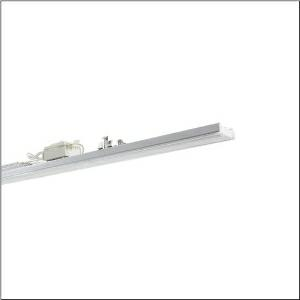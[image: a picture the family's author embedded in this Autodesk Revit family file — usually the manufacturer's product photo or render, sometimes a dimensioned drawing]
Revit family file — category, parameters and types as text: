
# Revit family: licross_r__21_recessed_mo_52tl1edn48xg_af32
name_source: partatom
category: Lighting Fixtures
units: mm (PartAtom-declared; Revit-internal decimal feet)

## family parameters
Cut with Voids When Loaded = No
Host = Face
Light Source = No
Part Type = Normal
Room Calculation Point = No
Round Connector Dimension = Use Diameter
Shared = No

## types (1)
- --- (1 x LED, 8000 lm, 45.8 W, 4000K)
    Apparent Load = 46 VA
    CIE Flux Codes = 85 95 99 100 100
    Color Rendering = 80
    Color Temperature = 4000K
    Default Elevation = 1800 mm
    Description = Licross® 21 Recessed MO, luminaire insert, of sheet steel, galvanised, coil coated, white, length: 1.500mm, width: 66mm, height: 67mm, LED rated luminous flux: 8.000lm, light colour: 840, control gear: DALI 2, with plug, 5-pole, with phase selection, mains connection: 220..240V, AC, 50/60Hz, rated input power: 46W, halogen-free wiring, primary light control with lens, of plastic, primary optical cover: cover, of PMMA, light emission: direct distribution, primary light characteristic: symmetric, protection rating (complete): IP40, insulation class (complete): insulation class I (protective earthing), certification: CE, ENEC, VDE, UKCA, protection symbol: D if used in an environment without relevant dust loads with corresponding accessories, impact resistance: IK06, permissible ambient temperature for indoor applications: -25..+40°C, corresponds to IFS (International Featured Standards) requirements for safety and quality in the food industry, reducing of maximum allowable ambient temperature of 5°C with ceiling mounting, LABS conformity tested according to VDMA 24364:2018-05, packaging unit: 1 piece
    Height = 58 mm
    Lamp = 1 x LED
    Lamp Light Flux = 8000 lm
    Lamp Power = 45.8 W
    Lamp count = 1
    Length = 1500 mm
    Luminous efficacy = 175 lm/W
    Manufacturer = Siteco
    ModVariant = No
    Model = 52TL1EDN48XG
    Mounting Place = Ceiling
    Mounting Type = Pendant
    Number of Poles = 1
    OnlyDefault = Yes
    Power Factor = 1
    Product Name = Licross® 21 Recessed MO
    Product group = luminaire insert
    ProductGroupID = 902
    Protection Class = Protection class I
    Protection Degree = IP 40
    RLX_Detail_Level = 1
    RLX_Emergency_Light_Flux = 0 lm
    RLX_Emergency_Type = 0
    RLX_Emergency_Type_DB = No
    RlxData = <blob elided: 24677 chars, md5=c9c32c79>
    Socket = socket
    Standby Power = 0 W
    System Light Flux = 8000 lm
    System Power = 46 W
    Type Comments = factory setting: luminous flux: 100 % | dim-lin: 254 | 308 mA
    Type Image = l_1296930.jpg
    URL = http://relux.com
    VarID = @adj_125262
    Voltage = 0 V
    Weight = 0.00 kg
    Width = 66 mm

## geometry (parser evidence)
native form markers: Blend x4, Sweep x11
no freeform markers — native parametric forms only
